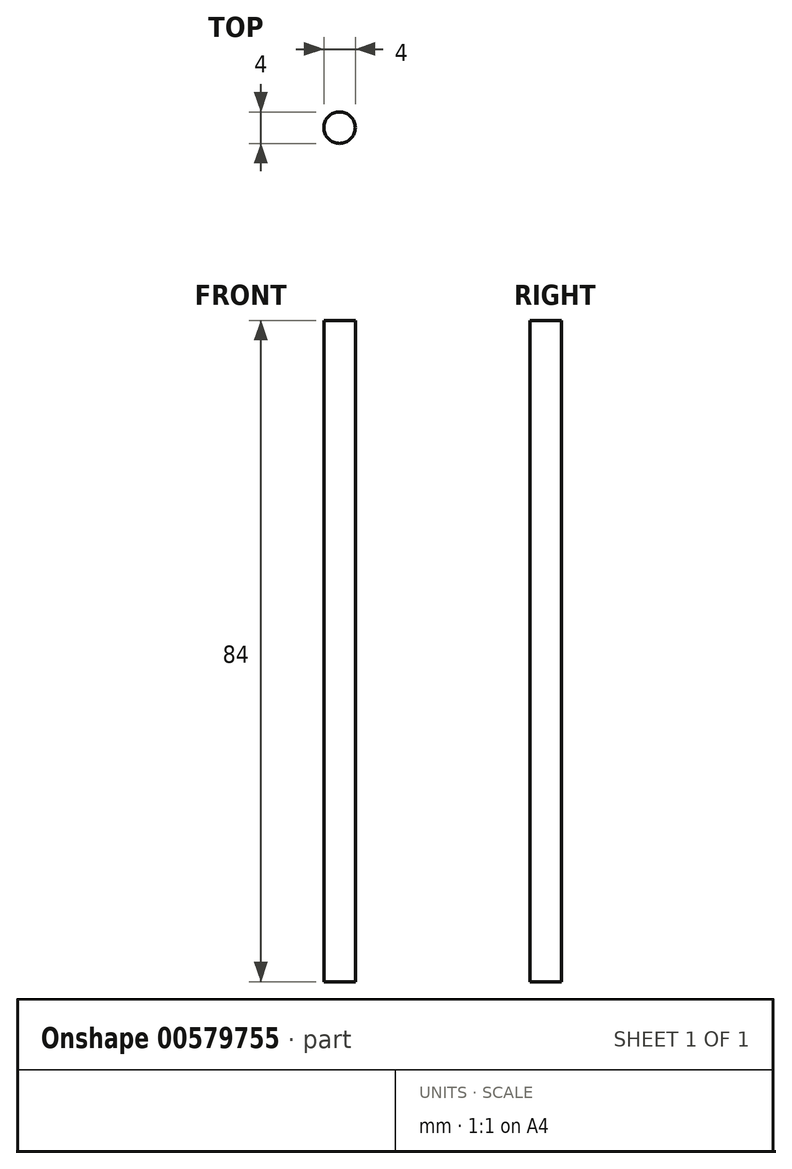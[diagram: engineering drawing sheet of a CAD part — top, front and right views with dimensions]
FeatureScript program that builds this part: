
annotation { "Feature Type Name" : "Feature", "Feature Type Description" : "" }
export const myFeature = defineFeature(function(context is Context, id is Id, definition is map)
    precondition{}
    {
        {
            var Q0;
            Q0=qCreatedBy(makeId("Top.planeOp"),FACE);
            var sketch = newSketch(context, id + "F0", { "sketchPlane" : qUnion([Q0])});
            skCircle(sketch, "E0", {"center": v(0, 0) * mm, "radius": 2 * mm});
            skSolve(sketch);
        }
        {
            var Q0;
            Q0=qSketchRegion(id+"F0",true);
            extrude(context, id + "F1", {"entities" : qUnion([Q0]), "oppositeDirection" : true, "depth" : 84 * mm, "offsetDistance" : 25 * mm});
        }
    });
